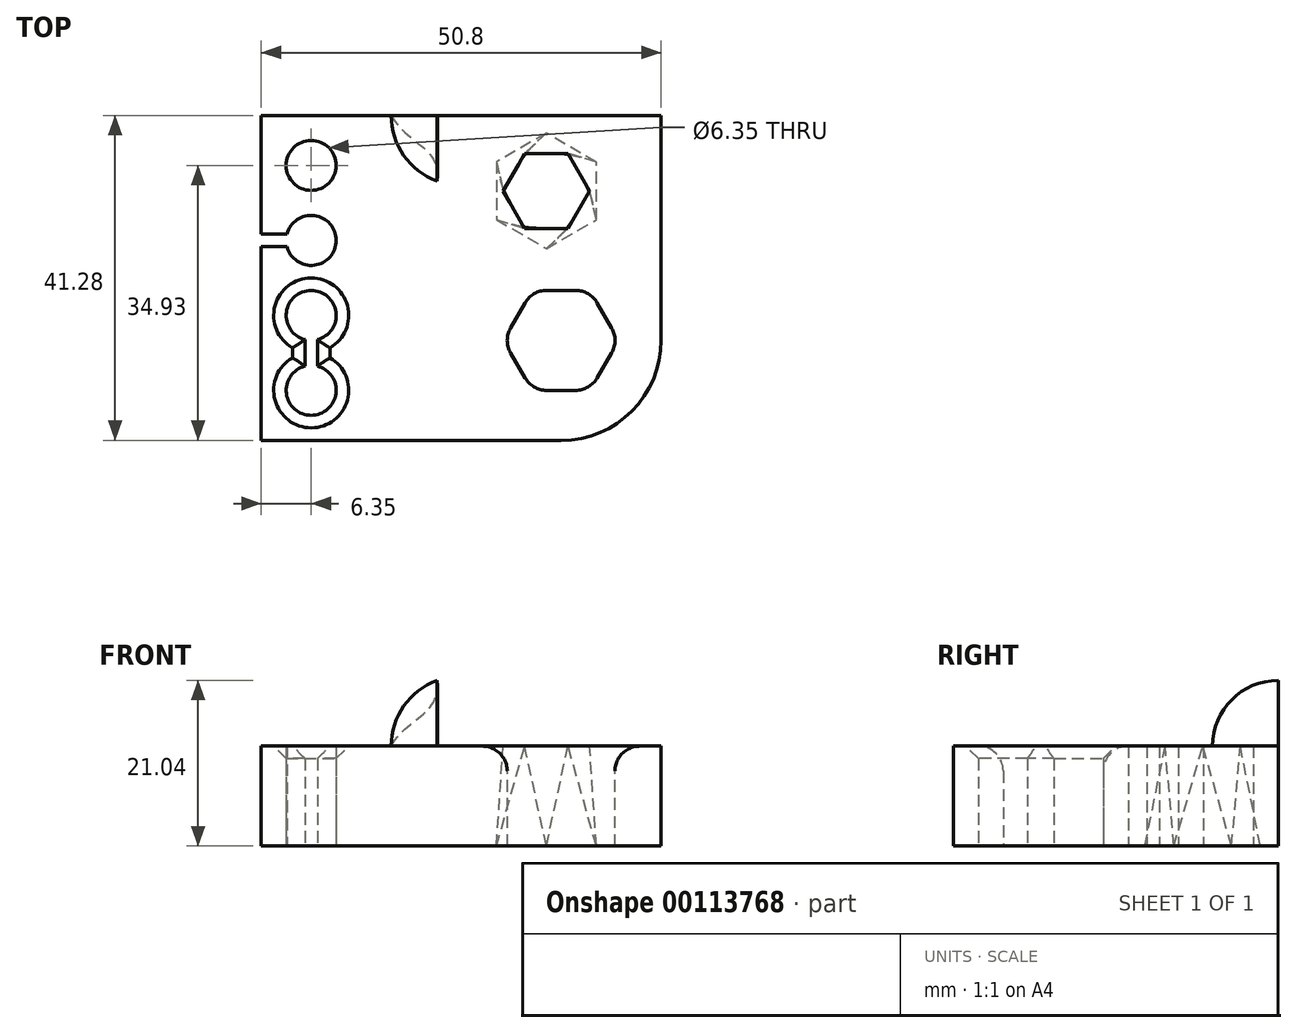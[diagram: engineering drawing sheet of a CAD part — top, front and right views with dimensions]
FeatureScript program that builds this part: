
annotation { "Feature Type Name" : "Feature", "Feature Type Description" : "" }
export const myFeature = defineFeature(function(context is Context, id is Id, definition is map)
    precondition{}
    {
        {
            var Q0;
            Q0=qCreatedBy(makeId("Top.planeOp"),FACE);
            var sketch = newSketch(context, id + "F0", { "sketchPlane" : qUnion([Q0])});
            skLineSegment(sketch, "E0.bottom", {"start": v(0, 0) * mm, "end": v(50.8, 0) * mm});
            skLineSegment(sketch, "E0.top", {"start": v(0, -41.27) * mm, "end": v(50.8, -41.27) * mm});
            skLineSegment(sketch, "E0.left", {"start": v(0, 0) * mm, "end": v(0, -41.27) * mm});
            skLineSegment(sketch, "E0.right", {"start": v(50.8, 0) * mm, "end": v(50.8, -41.28) * mm});
            skArc(sketch, "E1", {"start": v(5.56, -31.85) * mm, "mid": v(6.35, -38.1) * mm, "end": v(7.14, -31.85) * mm});
            skArc(sketch, "E2.0.1.0", {"start": v(7.14, -28.47) * mm, "mid": v(6.35, -22.23) * mm, "end": v(5.56, -28.47) * mm});
            skArc(sketch, "E2.0.2.0", {"start": v(3.28, -16.67) * mm, "mid": v(9.53, -15.88) * mm, "end": v(3.28, -15.08) * mm});
            skCircle(sketch, "E2.0.3.0", {"center": v(6.35, -6.35) * mm, "radius": 3.18 * mm});
            skLineSegment(sketch, "E2.direction1", {"start": v(6.35, -34.93) * mm, "end": v(31.75, -34.93) * mm, "construction": true});
            skLineSegment(sketch, "E2.direction2", {"start": v(6.35, -34.93) * mm, "end": v(6.35, -25.4) * mm, "construction": true});
            skLineSegment(sketch, "E3", {"start": v(6.35, -34.93) * mm, "end": v(5.56, -34.93) * mm});
            skLineSegment(sketch, "E4.MirrorCS", {"start": v(6.35, -34.93) * mm, "end": v(7.14, -34.93) * mm});
            skLineSegment(sketch, "E5", {"start": v(5.56, -34.93) * mm, "end": v(5.56, -25.4) * mm});
            skLineSegment(sketch, "E6", {"start": v(5.56, -25.4) * mm, "end": v(7.14, -25.4) * mm});
            skLineSegment(sketch, "E7", {"start": v(7.14, -25.4) * mm, "end": v(7.14, -34.93) * mm});
            skLineSegment(sketch, "E8", {"start": v(6.35, -15.88) * mm, "end": v(6.35, -15.08) * mm});
            skLineSegment(sketch, "E9", {"start": v(6.35, -15.88) * mm, "end": v(11.9, -15.88) * mm, "construction": true});
            skLineSegment(sketch, "E10.MirrorCS", {"start": v(6.35, -15.88) * mm, "end": v(6.35, -16.67) * mm});
            skLineSegment(sketch, "E11", {"start": v(6.35, -15.08) * mm, "end": v(0, -15.08) * mm});
            skLineSegment(sketch, "E12", {"start": v(6.35, -16.67) * mm, "end": v(0, -16.67) * mm});
            skCircle(sketch, "E13.cCircle", {"center": v(38.1, -28.58) * mm, "radius": 6.35 * mm, "construction": true});
            skLineSegment(sketch, "E13.0", {"start": v(41.77, -22.22) * mm, "end": v(45.43, -28.57) * mm});
            skLineSegment(sketch, "E13.1", {"start": v(45.43, -28.58) * mm, "end": v(41.77, -34.93) * mm});
            skLineSegment(sketch, "E13.2", {"start": v(41.77, -34.93) * mm, "end": v(34.43, -34.93) * mm});
            skLineSegment(sketch, "E13.3", {"start": v(34.43, -34.93) * mm, "end": v(30.77, -28.58) * mm});
            skLineSegment(sketch, "E13.4", {"start": v(30.77, -28.57) * mm, "end": v(34.43, -22.22) * mm});
            skLineSegment(sketch, "E13.5", {"start": v(34.43, -22.22) * mm, "end": v(41.77, -22.22) * mm});
            skPoint(sketch, "E13.0.midPoint", {"position": v(43.6, -25.4) * mm});
            skSolve(sketch);
        }
        {
            var Q0;
            {var subQ1=sQuery(id+"F0.wireOp",EDGE,"E0.bottom");Q0=makeQuery(id+"F0.imprint","IMPRINT",FACE,{"disambiguationData":[TD([[makeQuery(id+"F0.imprint","IMPRINT",EDGE,{"derivedFrom":subQ1}),-1.0]])]});}
            extrude(context, id + "F1", {"entities" : qUnion([Q0]), "depth" : 12.7 * mm});
        }
        {
            var Q0;
            Q0=makeQuery(id+"F1.opExtrude","SWEPT_EDGE",EDGE,{"disambiguationData":[OSD([sQuery(id+"F0.wireOp",EDGE,"E0.top"),sQuery(id+"F0.wireOp",EDGE,"E0.right")])]});
            fillet(context, id + "F2", {"entities" : qUnion([Q0]), "radius" : 12.7 * mm, "tangentPropagation" : true, "allowEdgeOverflow" : false});
        }
        {
            var Q0;
            Q0=makeQuery(id+"F1.opExtrude","CAP_EDGE",EDGE,{"disambiguationData":[OSD([sQuery(id+"F0.wireOp",EDGE,"E2.0.1.0")])],"isStart":false});
            var Q1;
            Q1=makeQuery(id+"F1.opExtrude","CAP_EDGE",EDGE,{"disambiguationData":[OSD([sQuery(id+"F0.wireOp",EDGE,"E7")])],"isStart":false});
            var Q2;
            Q2=makeQuery(id+"F1.opExtrude","CAP_EDGE",EDGE,{"disambiguationData":[OSD([sQuery(id+"F0.wireOp",EDGE,"E5")])],"isStart":false});
            var Q3;
            Q3=makeQuery(id+"F1.opExtrude","CAP_EDGE",EDGE,{"disambiguationData":[OSD([sQuery(id+"F0.wireOp",EDGE,"E1")])],"isStart":false});
            chamfer(context, id + "F3", {"entities" : qUnion([Q0, Q1, Q2, Q3]), "width" : 1.59 * mm, "tangentPropagation" : true});
        }
        {
            var Q0;
            Q0=makeQuery(id+"F1.opExtrude","CAP_EDGE",EDGE,{"disambiguationData":[OSD([sQuery(id+"F0.wireOp",EDGE,"E13.0")])],"isStart":false});
            var Q1;
            Q1=makeQuery(id+"F1.opExtrude","CAP_EDGE",EDGE,{"disambiguationData":[OSD([sQuery(id+"F0.wireOp",EDGE,"E13.3")])],"isStart":false});
            var Q2;
            Q2=makeQuery(id+"F1.opExtrude","CAP_EDGE",EDGE,{"disambiguationData":[OSD([sQuery(id+"F0.wireOp",EDGE,"E13.4")])],"isStart":false});
            var Q3;
            Q3=makeQuery(id+"F1.opExtrude","SWEPT_EDGE",EDGE,{"disambiguationData":[OSD([sQuery(id+"F0.wireOp",EDGE,"E13.2"),sQuery(id+"F0.wireOp",EDGE,"E13.3")])]});
            var Q4;
            Q4=makeQuery(id+"F1.opExtrude","SWEPT_EDGE",EDGE,{"disambiguationData":[OSD([sQuery(id+"F0.wireOp",EDGE,"E13.3"),sQuery(id+"F0.wireOp",EDGE,"E13.4")])]});
            var Q5;
            Q5=makeQuery(id+"F1.opExtrude","CAP_EDGE",EDGE,{"disambiguationData":[OSD([sQuery(id+"F0.wireOp",EDGE,"E13.2")])],"isStart":false});
            var Q6;
            Q6=makeQuery(id+"F1.opExtrude","CAP_EDGE",EDGE,{"disambiguationData":[OSD([sQuery(id+"F0.wireOp",EDGE,"E13.1")])],"isStart":false});
            var Q7;
            Q7=makeQuery(id+"F1.opExtrude","CAP_EDGE",EDGE,{"disambiguationData":[OSD([sQuery(id+"F0.wireOp",EDGE,"E13.5")])],"isStart":false});
            var Q8;
            Q8=makeQuery(id+"F1.opExtrude","SWEPT_EDGE",EDGE,{"disambiguationData":[OSD([sQuery(id+"F0.wireOp",EDGE,"E13.4"),sQuery(id+"F0.wireOp",EDGE,"E13.5")])]});
            var Q9;
            Q9=makeQuery(id+"F1.opExtrude","SWEPT_EDGE",EDGE,{"disambiguationData":[OSD([sQuery(id+"F0.wireOp",EDGE,"E13.0"),sQuery(id+"F0.wireOp",EDGE,"E13.5")])]});
            var Q10;
            Q10=makeQuery(id+"F1.opExtrude","SWEPT_EDGE",EDGE,{"disambiguationData":[OSD([sQuery(id+"F0.wireOp",EDGE,"E13.0"),sQuery(id+"F0.wireOp",EDGE,"E13.1")])]});
            var Q11;
            Q11=makeQuery(id+"F1.opExtrude","SWEPT_EDGE",EDGE,{"disambiguationData":[OSD([sQuery(id+"F0.wireOp",EDGE,"E13.1"),sQuery(id+"F0.wireOp",EDGE,"E13.2")])]});
            fillet(context, id + "F4", {"entities" : qUnion([Q0, Q1, Q2, Q3, Q4, Q5, Q6, Q7, Q8, Q9, Q10, Q11]), "radius" : 3.17 * mm, "tangentPropagation" : true, "allowEdgeOverflow" : false});
        }
        {
            var Q0;
            Q0=makeQuery(id+"F1.opExtrude","CAP_FACE",FACE,{"disambiguationData":[OSD([sQuery(id+"F0.wireOp",EDGE,"E0.bottom"),sQuery(id+"F0.wireOp",EDGE,"E0.top"),sQuery(id+"F0.wireOp",EDGE,"E0.left"),sQuery(id+"F0.wireOp",EDGE,"E0.right"),sQuery(id+"F0.wireOp",EDGE,"E1"),sQuery(id+"F0.wireOp",EDGE,"E2.0.1.0"),sQuery(id+"F0.wireOp",EDGE,"E2.0.2.0"),sQuery(id+"F0.wireOp",EDGE,"E2.0.3.0"),sQuery(id+"F0.wireOp",EDGE,"E5"),sQuery(id+"F0.wireOp",EDGE,"E7"),sQuery(id+"F0.wireOp",EDGE,"E11"),sQuery(id+"F0.wireOp",EDGE,"E12"),sQuery(id+"F0.wireOp",EDGE,"E13.0"),sQuery(id+"F0.wireOp",EDGE,"E13.1"),sQuery(id+"F0.wireOp",EDGE,"E13.2"),sQuery(id+"F0.wireOp",EDGE,"E13.3"),sQuery(id+"F0.wireOp",EDGE,"E13.4"),sQuery(id+"F0.wireOp",EDGE,"E13.5")])],"isStart":false});
            var sketch = newSketch(context, id + "F5", { "sketchPlane" : qUnion([Q0])});
            skCircle(sketch, "E14.cCircle", {"center": v(36.23, -9.58) * mm, "radius": 4.76 * mm, "construction": true});
            skLineSegment(sketch, "E14.0", {"start": v(30.73, -9.58) * mm, "end": v(33.48, -4.82) * mm});
            skLineSegment(sketch, "E14.1", {"start": v(33.48, -4.82) * mm, "end": v(38.98, -4.82) * mm});
            skLineSegment(sketch, "E14.2", {"start": v(38.98, -4.82) * mm, "end": v(41.73, -9.58) * mm});
            skLineSegment(sketch, "E14.3", {"start": v(41.73, -9.58) * mm, "end": v(38.98, -14.34) * mm});
            skLineSegment(sketch, "E14.4", {"start": v(38.98, -14.34) * mm, "end": v(33.48, -14.34) * mm});
            skLineSegment(sketch, "E14.5", {"start": v(33.48, -14.34) * mm, "end": v(30.73, -9.58) * mm});
            skPoint(sketch, "E14.0.midPoint", {"position": v(32.1, -7.2) * mm});
            skSolve(sketch);
        }
        {
            var Q0;
            Q0=makeQuery(id+"F1.opExtrude","CAP_FACE",FACE,{"disambiguationData":[OSD([sQuery(id+"F0.wireOp",EDGE,"E0.bottom"),sQuery(id+"F0.wireOp",EDGE,"E0.top"),sQuery(id+"F0.wireOp",EDGE,"E0.left"),sQuery(id+"F0.wireOp",EDGE,"E0.right"),sQuery(id+"F0.wireOp",EDGE,"E1"),sQuery(id+"F0.wireOp",EDGE,"E2.0.1.0"),sQuery(id+"F0.wireOp",EDGE,"E2.0.2.0"),sQuery(id+"F0.wireOp",EDGE,"E2.0.3.0"),sQuery(id+"F0.wireOp",EDGE,"E5"),sQuery(id+"F0.wireOp",EDGE,"E7"),sQuery(id+"F0.wireOp",EDGE,"E11"),sQuery(id+"F0.wireOp",EDGE,"E12"),sQuery(id+"F0.wireOp",EDGE,"E13.0"),sQuery(id+"F0.wireOp",EDGE,"E13.1"),sQuery(id+"F0.wireOp",EDGE,"E13.2"),sQuery(id+"F0.wireOp",EDGE,"E13.3"),sQuery(id+"F0.wireOp",EDGE,"E13.4"),sQuery(id+"F0.wireOp",EDGE,"E13.5")])],"isStart":true});
            var sketch = newSketch(context, id + "F6", { "sketchPlane" : qUnion([Q0])});
            skPoint(sketch, "E15.0", {"position": v(36.23, 9.58) * mm});
            skCircle(sketch, "E16.cCircle", {"center": v(36.23, 9.58) * mm, "radius": 6.35 * mm, "construction": true});
            skLineSegment(sketch, "E16.0", {"start": v(42.58, 13.25) * mm, "end": v(42.58, 5.91) * mm});
            skLineSegment(sketch, "E16.1", {"start": v(42.58, 5.91) * mm, "end": v(36.23, 2.25) * mm});
            skLineSegment(sketch, "E16.2", {"start": v(36.23, 2.25) * mm, "end": v(29.88, 5.91) * mm});
            skLineSegment(sketch, "E16.3", {"start": v(29.88, 5.91) * mm, "end": v(29.88, 13.25) * mm});
            skLineSegment(sketch, "E16.4", {"start": v(29.88, 13.25) * mm, "end": v(36.23, 16.91) * mm});
            skLineSegment(sketch, "E16.5", {"start": v(36.23, 16.91) * mm, "end": v(42.58, 13.25) * mm});
            skPoint(sketch, "E16.0.midPoint", {"position": v(42.58, 9.58) * mm});
            skSolve(sketch);
        }
        {
            var Q1;
            Q1=makeQuery(id+"F6.imprint","IMPRINT",FACE,{"disambiguationData":[TD([[makeQuery(id+"F6.imprint","IMPRINT",EDGE,{"derivedFrom":sQuery(id+"F6.wireOp",EDGE,"E16.0")}),-1.0]])]});
            var Q2;
            Q2=makeQuery(id+"F5.imprint","IMPRINT",FACE,{"disambiguationData":[TD([[makeQuery(id+"F5.imprint","IMPRINT",EDGE,{"derivedFrom":sQuery(id+"F5.wireOp",EDGE,"E14.0")}),-1.0]])]});
            loft(context, id + "F7", {"operationType" : NewBodyOperationType.REMOVE, "sheetProfilesArray" : [{ "sheetProfileEntities" : qUnion([Q1]) }, { "sheetProfileEntities" : qUnion([Q2]) }]});
        }
        {
            var Q0;
            Q0=makeQuery(id+"F1.opExtrude","SWEPT_FACE",FACE,{"disambiguationData":[OSD([sQuery(id+"F0.wireOp",EDGE,"E0.bottom")])]});
            var sketch = newSketch(context, id + "F8", { "sketchPlane" : qUnion([Q0])});
            skArc(sketch, "E17", {"start": v(-16.51, 12.7) * mm, "mid": v(-25.4, 21.59) * mm, "end": v(-34.3, 12.7) * mm});
            skLineSegment(sketch, "E18.0", {"start": v(0, 12.7) * mm, "end": v(-50.8, 12.7) * mm});
            skLineSegment(sketch, "E19", {"start": v(-34.3, 12.7) * mm, "end": v(-16.51, 12.7) * mm});
            skFitSpline(sketch, "E20", {"points": [v(-16.51, 12.7) * mm, v(-22.32, 21.04) * mm], "startDerivative": vector(-5.78, 10.64) * mm, "endDerivative": vector(1.95, 12.8) * mm});
            skSolve(sketch);
        }
        {
            var Q0;
            {var subQ0=sQuery(id+"F8.wireOp",EDGE,"E19");Q0=makeQuery(id+"F8.imprint","IMPRINT",FACE,{"disambiguationData":[TD([[makeQuery(id+"F8.imprint","IMPRINT",EDGE,{"derivedFrom":subQ0}),-1.0]])]});}
            var Q1;
            {var subQ0=sQuery(id+"F8.wireOp",EDGE,"E20");Q1=makeQuery(id+"F8.imprint","IMPRINT",FACE,{"disambiguationData":[TD([[makeQuery(id+"F8.imprint","IMPRINT",EDGE,{"derivedFrom":subQ0}),-1.0]])]});}
            var Q2;
            Q2=sQuery(id+"F8.wireOp",EDGE,"E18.0");
            revolve(context, id + "F9", {"operationType" : NewBodyOperationType.ADD, "entities" : qUnion([Q0, Q1]), "axis" : qUnion([Q2]), "revolveType" : RevolveType.ONE_DIRECTION, "angle" : 90 * degree});
        }
    });
